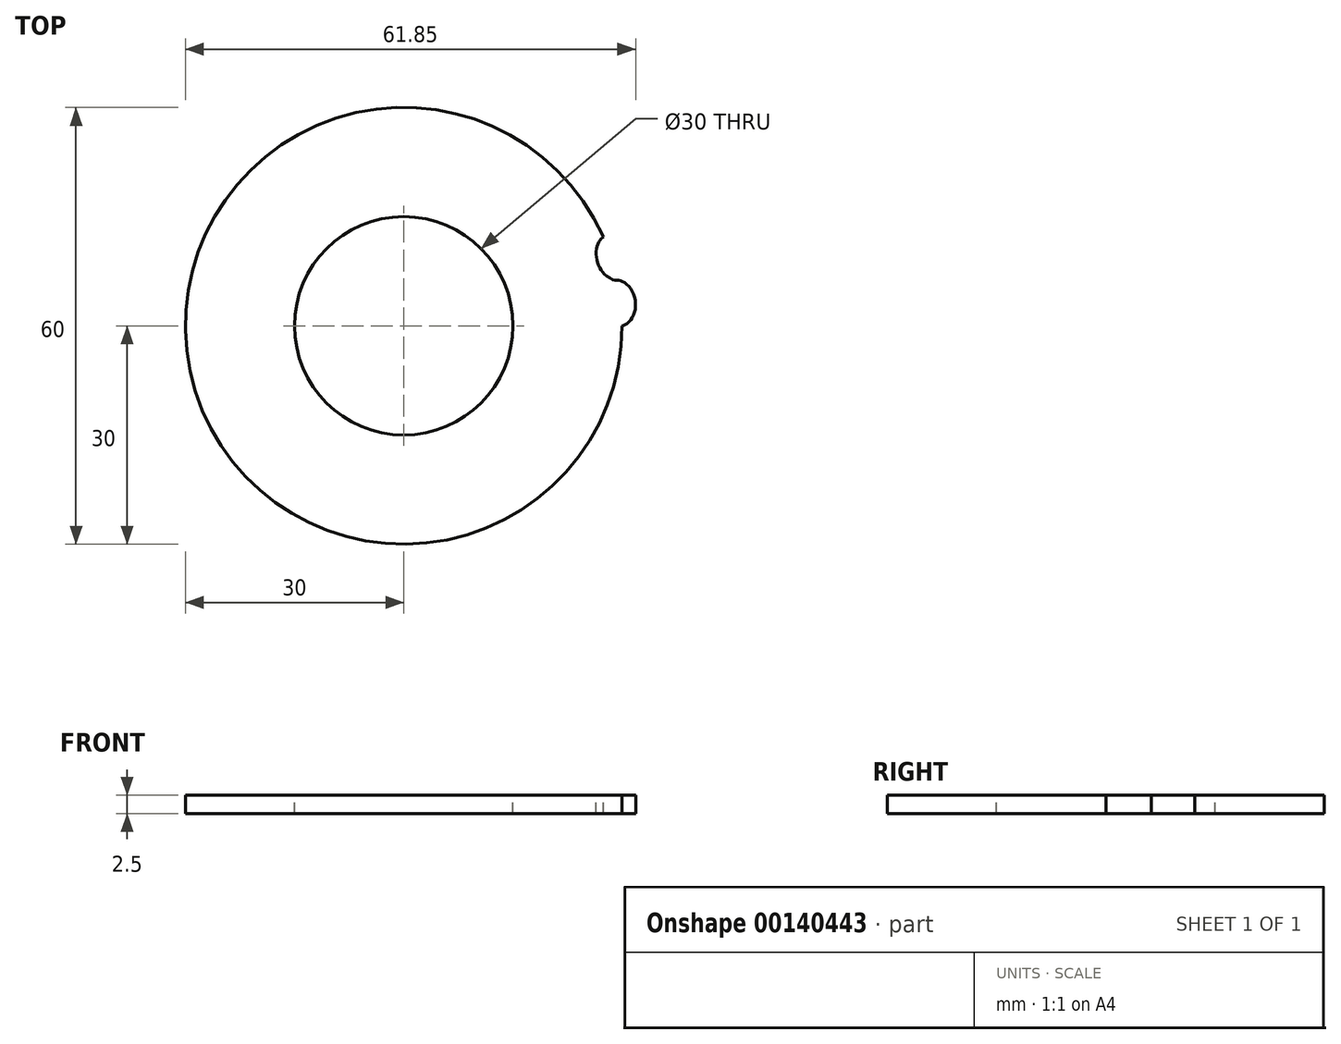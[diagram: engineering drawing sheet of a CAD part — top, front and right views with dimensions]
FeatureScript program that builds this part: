
annotation { "Feature Type Name" : "Feature", "Feature Type Description" : "" }
export const myFeature = defineFeature(function(context is Context, id is Id, definition is map)
    precondition{}
    {
        {
            assignVariable(context, id + "F0", {"name" : "t", "anyValue" : 2.5});
        }
        {
            var Q0;
            Q0=qCreatedBy(makeId("Top.planeOp"),FACE);
            var sketch = newSketch(context, id + "F1", { "sketchPlane" : qUnion([Q0])});
            skCircle(sketch, "E0", {"center": v(0, 0) * mm, "radius": 30 * mm});
            skSolve(sketch);
        }
        {
            var Q0;
            Q0 = qSketchRegion(id + "F1", true);
            extrude(context, id + "F2", {"entities" : qUnion([Q0]), "depth" : (getVariable(context, 't')) * mm});
        }
        {
            var Q0;
            Q0=makeQuery(id+"F2.opExtrude","CAP_FACE",FACE,{"disambiguationData":[OSD([sQuery(id+"F1.wireOp",EDGE,"E0")])],"isStart":false});
            var sketch = newSketch(context, id + "F3", { "sketchPlane" : qUnion([Q0])});
            skLineSegment(sketch, "E1", {"start": v(0, 0) * mm, "end": v(29.34, 6.24) * mm, "construction": true});
            skLineSegment(sketch, "E2", {"start": v(29.34, 6.24) * mm, "end": v(31.3, 6.65) * mm, "construction": true});
            skPoint(sketch, "E3", {"position": v(30.32, 6.45) * mm});
            skCircle(sketch, "E4", {"center": v(30.32, 6.45) * mm, "radius": 1 * mm, "construction": true});
            skLineSegment(sketch, "E5", {"start": v(30, 0) * mm, "end": v(31, 0) * mm, "construction": true});
            skLineSegment(sketch, "E6", {"start": v(30.32, 6.45) * mm, "end": v(29.58, 5.78) * mm, "construction": true});
            skLineSegment(sketch, "E7", {"start": v(30.32, 6.45) * mm, "end": v(31.07, 7.11) * mm, "construction": true});
            skLineSegment(sketch, "E8", {"start": v(30.32, 6.45) * mm, "end": v(29.37, 6.75) * mm, "construction": true});
            skLineSegment(sketch, "E9", {"start": v(30.32, 6.45) * mm, "end": v(31.27, 6.14) * mm, "construction": true});
            skLineSegment(sketch, "E10", {"start": v(30.32, 6.45) * mm, "end": v(30.01, 5.5) * mm, "construction": true});
            skLineSegment(sketch, "E11", {"start": v(30.32, 6.45) * mm, "end": v(30.53, 5.47) * mm, "construction": true});
            skLineSegment(sketch, "E12", {"start": v(30.32, 6.45) * mm, "end": v(31, 5.7) * mm, "construction": true});
            skLineSegment(sketch, "E13", {"start": v(30.32, 6.45) * mm, "end": v(30.63, 7.4) * mm, "construction": true});
            skLineSegment(sketch, "E14", {"start": v(30.32, 6.45) * mm, "end": v(30.11, 7.42) * mm, "construction": true});
            skLineSegment(sketch, "E15", {"start": v(30.32, 6.45) * mm, "end": v(29.65, 7.19) * mm, "construction": true});
            skArc(sketch, "E16", {"start": v(31, 0) * mm, "mid": v(30.83, 3.24) * mm, "end": v(30.32, 6.45) * mm, "construction": true});
            skLineSegment(sketch, "E17", {"start": v(30.43, 5.92) * mm, "end": v(0, 0) * mm, "construction": true});
            skLineSegment(sketch, "E18", {"start": v(0, 0) * mm, "end": v(30.53, 5.38) * mm, "construction": true});
            skLineSegment(sketch, "E19", {"start": v(0, 0) * mm, "end": v(30.62, 4.85) * mm, "construction": true});
            skLineSegment(sketch, "E20", {"start": v(0, 0) * mm, "end": v(30.7, 4.31) * mm, "construction": true});
            skLineSegment(sketch, "E21", {"start": v(0, 0) * mm, "end": v(30.77, 3.78) * mm, "construction": true});
            skLineSegment(sketch, "E22", {"start": v(0, 0) * mm, "end": v(30.83, 3.24) * mm, "construction": true});
            skLineSegment(sketch, "E23", {"start": v(0, 0) * mm, "end": v(30.88, 2.7) * mm, "construction": true});
            skLineSegment(sketch, "E24", {"start": v(0, 0) * mm, "end": v(30.92, 2.16) * mm, "construction": true});
            skLineSegment(sketch, "E25", {"start": v(0, 0) * mm, "end": v(30.96, 1.62) * mm, "construction": true});
            skLineSegment(sketch, "E26", {"start": v(0, 0) * mm, "end": v(30.98, 1.08) * mm, "construction": true});
            skLineSegment(sketch, "E27", {"start": v(0, 0) * mm, "end": v(31, 0.54) * mm, "construction": true});
            skLineSegment(sketch, "E28", {"start": v(0, 0) * mm, "end": v(31, 0) * mm, "construction": true});
            skLineSegment(sketch, "E29", {"start": v(31, 0) * mm, "end": v(31.87, 0) * mm, "construction": true});
            skArc(sketch, "E30", {"start": v(29.37, 6.75) * mm, "mid": v(29.95, 3.4) * mm, "end": v(30.14, 0) * mm, "construction": true});
            skArc(sketch, "E31", {"start": v(29.65, 7.19) * mm, "mid": v(30.3, 3.62) * mm, "end": v(30.51, 0) * mm, "construction": true});
            skArc(sketch, "E32", {"start": v(30.11, 7.42) * mm, "mid": v(30.79, 3.74) * mm, "end": v(31.02, 0) * mm, "construction": true});
            skArc(sketch, "E33", {"start": v(30.63, 7.4) * mm, "mid": v(31.3, 3.72) * mm, "end": v(31.51, 0) * mm, "construction": true});
            skArc(sketch, "E34", {"start": v(31.07, 7.11) * mm, "mid": v(31.67, 3.58) * mm, "end": v(31.87, 0) * mm, "construction": true});
            skPoint(sketch, "E35", {"position": v(29.95, 5.82) * mm});
            skPoint(sketch, "E36", {"position": v(30.43, 5.92) * mm});
            skLineSegment(sketch, "E37", {"start": v(30.43, 5.92) * mm, "end": v(29.48, 6.24) * mm, "construction": true});
            skLineSegment(sketch, "E38", {"start": v(30.53, 5.38) * mm, "end": v(29.89, 6.15) * mm, "construction": true});
            skLineSegment(sketch, "E39", {"start": v(30.62, 4.85) * mm, "end": v(30.46, 5.84) * mm, "construction": true});
            skLineSegment(sketch, "E40", {"start": v(30.7, 4.31) * mm, "end": v(31.07, 5.24) * mm, "construction": true});
            skArc(sketch, "E41", {"start": v(31.3, 6.65) * mm, "mid": v(31.82, 3.34) * mm, "end": v(32, 0) * mm, "construction": true});
            skLineSegment(sketch, "E42", {"start": v(30.77, 3.78) * mm, "end": v(31.57, 4.38) * mm, "construction": true});
            skLineSegment(sketch, "E43", {"start": v(30.83, 3.24) * mm, "end": v(31.82, 3.34) * mm, "construction": true});
            skLineSegment(sketch, "E44", {"start": v(30.88, 2.7) * mm, "end": v(31.79, 2.28) * mm, "construction": true});
            skLineSegment(sketch, "E45", {"start": v(30.92, 2.16) * mm, "end": v(31.48, 1.33) * mm, "construction": true});
            skLineSegment(sketch, "E46", {"start": v(30.96, 1.62) * mm, "end": v(31, 0.62) * mm, "construction": true});
            skLineSegment(sketch, "E47", {"start": v(30.98, 1.08) * mm, "end": v(30.51, 0.2) * mm, "construction": true});
            skLineSegment(sketch, "E48", {"start": v(31, 0.54) * mm, "end": v(30.14, 0.03) * mm, "construction": true});
            skFitSpline(sketch, "E49", {"points": [v(29.34, 6.24) * mm, v(29.48, 6.24) * mm, v(29.89, 6.15) * mm, v(30.46, 5.84) * mm, v(31.07, 5.24) * mm, v(31.57, 4.38) * mm, v(31.82, 3.34) * mm, v(31.79, 2.28) * mm, v(31.48, 1.33) * mm, v(31, 0.62) * mm, v(30.51, 0.2) * mm, v(30.14, 0.03) * mm, v(30, 0) * mm], "startDerivative": vector(3.74, 0.8) * mm, "endDerivative": vector(-3.82, 0) * mm});
            skArc(sketch, "E50.0", {"start": v(30, 0) * mm, "mid": v(29.84, 3.14) * mm, "end": v(29.34, 6.24) * mm});
            skArc(sketch, "E51", {"start": v(29.34, 6.24) * mm, "mid": v(29.4, 5.98) * mm, "end": v(29.45, 5.72) * mm});
            skArc(sketch, "E52", {"start": v(29.45, 5.72) * mm, "mid": v(29.5, 5.47) * mm, "end": v(29.54, 5.2) * mm});
            skLineSegment(sketch, "E53", {"start": v(-26.75, -3.74) * mm, "end": v(2.6, 2.5) * mm, "construction": true});
            skLineSegment(sketch, "E54", {"start": v(2.6, 2.5) * mm, "end": v(4.55, 2.91) * mm, "construction": true});
            skPoint(sketch, "E55", {"position": v(3.58, 2.7) * mm});
            skCircle(sketch, "E56", {"center": v(3.58, 2.7) * mm, "radius": 1 * mm, "construction": true});
            skLineSegment(sketch, "E57", {"start": v(3.25, -3.74) * mm, "end": v(4.25, -3.74) * mm, "construction": true});
            skLineSegment(sketch, "E58", {"start": v(3.58, 2.7) * mm, "end": v(2.83, 2.04) * mm, "construction": true});
            skLineSegment(sketch, "E59", {"start": v(3.58, 2.7) * mm, "end": v(4.32, 3.37) * mm, "construction": true});
            skLineSegment(sketch, "E60", {"start": v(3.58, 2.7) * mm, "end": v(2.62, 3.01) * mm, "construction": true});
            skLineSegment(sketch, "E61", {"start": v(3.58, 2.7) * mm, "end": v(4.53, 2.4) * mm, "construction": true});
            skLineSegment(sketch, "E62", {"start": v(3.58, 2.7) * mm, "end": v(3.27, 1.75) * mm, "construction": true});
            skLineSegment(sketch, "E63", {"start": v(3.58, 2.7) * mm, "end": v(3.78, 1.73) * mm, "construction": true});
            skLineSegment(sketch, "E64", {"start": v(3.58, 2.7) * mm, "end": v(4.24, 1.96) * mm, "construction": true});
            skLineSegment(sketch, "E65", {"start": v(3.58, 2.7) * mm, "end": v(3.88, 3.66) * mm, "construction": true});
            skLineSegment(sketch, "E66", {"start": v(3.58, 2.7) * mm, "end": v(3.37, 3.68) * mm, "construction": true});
            skLineSegment(sketch, "E67", {"start": v(3.58, 2.7) * mm, "end": v(2.9, 3.45) * mm, "construction": true});
            skArc(sketch, "E68", {"start": v(4.25, -3.74) * mm, "mid": v(4.08, -0.5) * mm, "end": v(3.58, 2.7) * mm, "construction": true});
            skLineSegment(sketch, "E69", {"start": v(3.68, 2.17) * mm, "end": v(-26.75, -3.74) * mm, "construction": true});
            skLineSegment(sketch, "E70", {"start": v(-26.75, -3.74) * mm, "end": v(3.78, 1.64) * mm, "construction": true});
            skLineSegment(sketch, "E71", {"start": v(-26.75, -3.74) * mm, "end": v(3.87, 1.1) * mm, "construction": true});
            skLineSegment(sketch, "E72", {"start": v(-26.75, -3.74) * mm, "end": v(3.95, 0.57) * mm, "construction": true});
            skLineSegment(sketch, "E73", {"start": v(-26.75, -3.74) * mm, "end": v(4.02, 0.04) * mm, "construction": true});
            skLineSegment(sketch, "E74", {"start": v(-26.75, -3.74) * mm, "end": v(4.08, -0.5) * mm, "construction": true});
            skLineSegment(sketch, "E75", {"start": v(-26.75, -3.74) * mm, "end": v(4.13, -1.04) * mm, "construction": true});
            skLineSegment(sketch, "E76", {"start": v(-26.75, -3.74) * mm, "end": v(4.18, -1.58) * mm, "construction": true});
            skLineSegment(sketch, "E77", {"start": v(-26.75, -3.74) * mm, "end": v(4.2, -2.12) * mm, "construction": true});
            skLineSegment(sketch, "E78", {"start": v(-26.75, -3.74) * mm, "end": v(4.23, -2.66) * mm, "construction": true});
            skLineSegment(sketch, "E79", {"start": v(-26.75, -3.74) * mm, "end": v(4.25, -3.2) * mm, "construction": true});
            skLineSegment(sketch, "E80", {"start": v(-26.75, -3.74) * mm, "end": v(4.25, -3.74) * mm, "construction": true});
            skLineSegment(sketch, "E81", {"start": v(4.25, -3.74) * mm, "end": v(5.12, -3.74) * mm, "construction": true});
            skArc(sketch, "E82", {"start": v(2.62, 3.01) * mm, "mid": v(3.2, -0.34) * mm, "end": v(3.4, -3.74) * mm, "construction": true});
            skArc(sketch, "E83", {"start": v(2.9, 3.45) * mm, "mid": v(3.55, -0.12) * mm, "end": v(3.76, -3.74) * mm, "construction": true});
            skArc(sketch, "E84", {"start": v(3.37, 3.68) * mm, "mid": v(4.04, 0) * mm, "end": v(4.27, -3.74) * mm, "construction": true});
            skArc(sketch, "E85", {"start": v(3.88, 3.66) * mm, "mid": v(4.54, -0.02) * mm, "end": v(4.76, -3.74) * mm, "construction": true});
            skArc(sketch, "E86", {"start": v(4.32, 3.37) * mm, "mid": v(4.92, -0.16) * mm, "end": v(5.12, -3.74) * mm, "construction": true});
            skPoint(sketch, "E87", {"position": v(3.2, 2.08) * mm});
            skPoint(sketch, "E88", {"position": v(3.68, 2.17) * mm});
            skLineSegment(sketch, "E89", {"start": v(3.68, 2.17) * mm, "end": v(2.74, 2.5) * mm, "construction": true});
            skLineSegment(sketch, "E90", {"start": v(3.78, 1.64) * mm, "end": v(3.14, 2.4) * mm, "construction": true});
            skLineSegment(sketch, "E91", {"start": v(3.87, 1.1) * mm, "end": v(3.71, 2.1) * mm, "construction": true});
            skLineSegment(sketch, "E92", {"start": v(3.95, 0.57) * mm, "end": v(4.33, 1.5) * mm, "construction": true});
            skArc(sketch, "E93", {"start": v(4.55, 2.91) * mm, "mid": v(5.08, -0.4) * mm, "end": v(5.25, -3.74) * mm, "construction": true});
            skLineSegment(sketch, "E94", {"start": v(4.02, 0.04) * mm, "end": v(4.82, 0.64) * mm, "construction": true});
            skLineSegment(sketch, "E95", {"start": v(4.08, -0.5) * mm, "end": v(5.08, -0.4) * mm, "construction": true});
            skLineSegment(sketch, "E96", {"start": v(4.13, -1.04) * mm, "end": v(5.04, -1.46) * mm, "construction": true});
            skLineSegment(sketch, "E97", {"start": v(4.18, -1.58) * mm, "end": v(4.74, -2.4) * mm, "construction": true});
            skLineSegment(sketch, "E98", {"start": v(4.2, -2.12) * mm, "end": v(4.26, -3.12) * mm, "construction": true});
            skLineSegment(sketch, "E99", {"start": v(4.23, -2.66) * mm, "end": v(3.76, -3.54) * mm, "construction": true});
            skLineSegment(sketch, "E100", {"start": v(4.25, -3.2) * mm, "end": v(3.4, -3.71) * mm, "construction": true});
            skFitSpline(sketch, "E101", {"points": [v(2.6, 2.5) * mm, v(2.74, 2.5) * mm, v(3.14, 2.4) * mm, v(3.71, 2.1) * mm, v(4.33, 1.5) * mm, v(4.82, 0.64) * mm, v(5.08, -0.4) * mm, v(5.04, -1.46) * mm, v(4.74, -2.4) * mm, v(4.26, -3.12) * mm, v(3.76, -3.54) * mm, v(3.4, -3.71) * mm, v(3.25, -3.74) * mm], "startDerivative": vector(3.74, 0.8) * mm, "endDerivative": vector(-3.82, 0) * mm});
            skArc(sketch, "E102.0", {"start": v(3.25, -3.74) * mm, "mid": v(3.09, -0.6) * mm, "end": v(2.6, 2.5) * mm});
            skArc(sketch, "E103", {"start": v(2.6, 2.5) * mm, "mid": v(2.65, 2.24) * mm, "end": v(2.7, 1.98) * mm});
            skArc(sketch, "E104", {"start": v(2.7, 1.98) * mm, "mid": v(2.75, 1.73) * mm, "end": v(2.8, 1.47) * mm});
            skSolve(sketch);
        }
        {
            var Q0;
            Q0 = qSketchRegion(id + "F3", true);
            var Q1;
            Q1=makeQuery(id+"F2.opExtrude","CAP_FACE",FACE,{"disambiguationData":[OSD([sQuery(id+"F1.wireOp",EDGE,"E0")])],"isStart":true});
            extrude(context, id + "F4", {"entities" : qUnion([Q0]), "operationType" : NewBodyOperationType.ADD, "endBound" : BoundingType.UP_TO_SURFACE, "oppositeDirection" : true, "endBoundEntityFace" : qUnion([Q1]), "depth" : 2.5 * mm});
        }
        {
            var Q0;
            {var subQ0=sQuery(id+"F3.wireOp",EDGE,"E50.0");Q0=makeQuery(id+"F3.imprint","IMPRINT",FACE,{"disambiguationData":[TD([[makeQuery(id+"F3.imprint","IMPRINT",EDGE,{"derivedFrom":subQ0}),1.0]])]});}
            var sketch = newSketch(context, id + "F5", { "sketchPlane" : qUnion([Q0])});
            skLineSegment(sketch, "E105.0", {"start": v(0, 0) * mm, "end": v(29.34, 6.24) * mm, "construction": true});
            skLineSegment(sketch, "E106.0.0", {"start": v(30, 0) * mm, "end": v(30, 0) * mm});
            skLineSegment(sketch, "E107", {"start": v(0, 0) * mm, "end": v(27.4, 12.2) * mm, "construction": true});
            skCircle(sketch, "E108", {"center": v(26.5, 11.8) * mm, "radius": 1 * mm, "construction": true});
            skArc(sketch, "E109", {"start": v(26.5, 11.8) * mm, "mid": v(27.58, 8.96) * mm, "end": v(28.37, 6.03) * mm, "construction": true});
            skLineSegment(sketch, "E110", {"start": v(26.5, 11.8) * mm, "end": v(26.9, 10.88) * mm, "construction": true});
            skArc(sketch, "E111", {"start": v(27.08, 12.6) * mm, "mid": v(28.33, 9.47) * mm, "end": v(29.22, 6.21) * mm, "construction": true});
            skArc(sketch, "E112", {"start": v(26.6, 12.79) * mm, "mid": v(27.93, 9.53) * mm, "end": v(28.87, 6.14) * mm, "construction": true});
            skArc(sketch, "E113", {"start": v(25.68, 12.38) * mm, "mid": v(26.98, 9.22) * mm, "end": v(27.9, 5.93) * mm, "construction": true});
            skArc(sketch, "E114", {"start": v(25.5, 11.9) * mm, "mid": v(26.68, 8.93) * mm, "end": v(27.52, 5.85) * mm, "construction": true});
            skArc(sketch, "E115", {"start": v(27.4, 12.2) * mm, "mid": v(27.51, 11.96) * mm, "end": v(27.62, 11.72) * mm});
            skLineSegment(sketch, "E116", {"start": v(27.62, 11.72) * mm, "end": v(0, 0) * mm, "construction": true});
            skArc(sketch, "E117", {"start": v(27.4, 12.2) * mm, "mid": v(28.53, 9.27) * mm, "end": v(29.34, 6.24) * mm});
            skLineSegment(sketch, "E118", {"start": v(0, 0) * mm, "end": v(27.82, 11.24) * mm, "construction": true});
            skLineSegment(sketch, "E119", {"start": v(0, 0) * mm, "end": v(28, 10.75) * mm, "construction": true});
            skLineSegment(sketch, "E120", {"start": v(0, 0) * mm, "end": v(28.2, 10.26) * mm, "construction": true});
            skLineSegment(sketch, "E121", {"start": v(0, 0) * mm, "end": v(28.37, 9.77) * mm, "construction": true});
            skLineSegment(sketch, "E122", {"start": v(0, 0) * mm, "end": v(28.53, 9.27) * mm, "construction": true});
            skLineSegment(sketch, "E123", {"start": v(0, 0) * mm, "end": v(28.69, 8.77) * mm, "construction": true});
            skLineSegment(sketch, "E124", {"start": v(0, 0) * mm, "end": v(28.84, 8.27) * mm, "construction": true});
            skLineSegment(sketch, "E125", {"start": v(28.98, 7.76) * mm, "end": v(0, 0) * mm, "construction": true});
            skLineSegment(sketch, "E126", {"start": v(0, 0) * mm, "end": v(29.1, 7.26) * mm, "construction": true});
            skLineSegment(sketch, "E127", {"start": v(0, 0) * mm, "end": v(29.23, 6.75) * mm, "construction": true});
            skLineSegment(sketch, "E128", {"start": v(26.7, 11.33) * mm, "end": v(27.3, 12.13) * mm, "construction": true});
            skLineSegment(sketch, "E129", {"start": v(26.89, 10.86) * mm, "end": v(27.03, 11.85) * mm, "construction": true});
            skArc(sketch, "E130", {"start": v(26.09, 12.7) * mm, "mid": v(27.44, 9.44) * mm, "end": v(28.38, 6.03) * mm, "construction": true});
            skLineSegment(sketch, "E131", {"start": v(27.07, 10.4) * mm, "end": v(26.72, 11.33) * mm, "construction": true});
            skLineSegment(sketch, "E132", {"start": v(27.25, 9.92) * mm, "end": v(26.49, 10.56) * mm, "construction": true});
            skLineSegment(sketch, "E133", {"start": v(27.42, 9.44) * mm, "end": v(26.44, 9.63) * mm, "construction": true});
            skLineSegment(sketch, "E134", {"start": v(27.58, 8.96) * mm, "end": v(26.63, 8.65) * mm, "construction": true});
            skArc(sketch, "E135", {"start": v(25.58, 11.39) * mm, "mid": v(26.63, 8.65) * mm, "end": v(27.39, 5.82) * mm, "construction": true});
            skLineSegment(sketch, "E136", {"start": v(27.73, 8.48) * mm, "end": v(27.05, 7.75) * mm, "construction": true});
            skLineSegment(sketch, "E137", {"start": v(27.88, 8) * mm, "end": v(27.63, 7.02) * mm, "construction": true});
            skLineSegment(sketch, "E138", {"start": v(28.14, 7.02) * mm, "end": v(28.83, 6.3) * mm, "construction": true});
            skLineSegment(sketch, "E139", {"start": v(28.26, 6.52) * mm, "end": v(29.21, 6.23) * mm, "construction": true});
            skFitSpline(sketch, "E140", {"points": [v(29.34, 6.24) * mm, v(29.21, 6.23) * mm, v(28.83, 6.3) * mm, v(27.63, 7.02) * mm, v(27.05, 7.75) * mm, v(26.63, 8.65) * mm, v(26.44, 9.63) * mm, v(26.49, 10.56) * mm, v(26.72, 11.33) * mm, v(27.03, 11.85) * mm, v(27.3, 12.13) * mm, v(27.4, 12.2) * mm], "startDerivative": vector(-3.54, -0.75) * mm, "endDerivative": vector(3.3, 1.47) * mm});
            skLineSegment(sketch, "E141", {"start": v(26.5, 11.8) * mm, "end": v(27.08, 12.6) * mm, "construction": true});
            skLineSegment(sketch, "E142", {"start": v(26.5, 11.8) * mm, "end": v(26.6, 12.79) * mm, "construction": true});
            skLineSegment(sketch, "E143", {"start": v(26.5, 11.8) * mm, "end": v(26.09, 12.7) * mm, "construction": true});
            skLineSegment(sketch, "E144", {"start": v(26.5, 11.8) * mm, "end": v(25.68, 12.38) * mm, "construction": true});
            skLineSegment(sketch, "E145", {"start": v(26.5, 11.8) * mm, "end": v(25.5, 11.9) * mm, "construction": true});
            skSolve(sketch);
        }
        {
            var Q0;
            Q0 = qSketchRegion(id + "F5", true);
            extrude(context, id + "F6", {"entities" : qUnion([Q0]), "operationType" : NewBodyOperationType.REMOVE, "endBound" : BoundingType.THROUGH_ALL, "oppositeDirection" : true, "depth" : 25 * mm});
        }
        {
            var Q0;
            {var subQ0=sQuery(id+"F3.wireOp",EDGE,"E52");var subQ1=sQuery(id+"F3.wireOp",EDGE,"E51");var subQ2=sQuery(id+"F3.wireOp",EDGE,"E50.0");var subQ3=sQuery(id+"F3.wireOp",EDGE,"E49");Q0=makeQuery(id+"FYuu5osC36glpG0_1.29.F4.boolean.opBoolean","MERGE",FACE,{"derivedFrom":[makeQuery(id+"FYuu5osC36glpG0_1.28.F4.boolean.opBoolean","MERGE",FACE,{"derivedFrom":[makeQuery(id+"FYuu5osC36glpG0_1.27.F4.boolean.opBoolean","MERGE",FACE,{"derivedFrom":[makeQuery(id+"FYuu5osC36glpG0_1.26.F4.boolean.opBoolean","MERGE",FACE,{"derivedFrom":[makeQuery(id+"FYuu5osC36glpG0_1.25.F4.boolean.opBoolean","MERGE",FACE,{"derivedFrom":[makeQuery(id+"FYuu5osC36glpG0_1.24.F4.boolean.opBoolean","MERGE",FACE,{"derivedFrom":[makeQuery(id+"FYuu5osC36glpG0_1.23.F4.boolean.opBoolean","MERGE",FACE,{"derivedFrom":[makeQuery(id+"FYuu5osC36glpG0_1.22.F4.boolean.opBoolean","MERGE",FACE,{"derivedFrom":[makeQuery(id+"FYuu5osC36glpG0_1.21.F4.boolean.opBoolean","MERGE",FACE,{"derivedFrom":[makeQuery(id+"FYuu5osC36glpG0_1.20.F4.boolean.opBoolean","MERGE",FACE,{"derivedFrom":[makeQuery(id+"FYuu5osC36glpG0_1.19.F4.boolean.opBoolean","MERGE",FACE,{"derivedFrom":[makeQuery(id+"FYuu5osC36glpG0_1.18.F4.boolean.opBoolean","MERGE",FACE,{"derivedFrom":[makeQuery(id+"FYuu5osC36glpG0_1.17.F4.boolean.opBoolean","MERGE",FACE,{"derivedFrom":[makeQuery(id+"FYuu5osC36glpG0_1.16.F4.boolean.opBoolean","MERGE",FACE,{"derivedFrom":[makeQuery(id+"FYuu5osC36glpG0_1.15.F4.boolean.opBoolean","MERGE",FACE,{"derivedFrom":[makeQuery(id+"FYuu5osC36glpG0_1.14.F4.boolean.opBoolean","MERGE",FACE,{"derivedFrom":[makeQuery(id+"FYuu5osC36glpG0_1.13.F4.boolean.opBoolean","MERGE",FACE,{"derivedFrom":[makeQuery(id+"FYuu5osC36glpG0_1.12.F4.boolean.opBoolean","MERGE",FACE,{"derivedFrom":[makeQuery(id+"FYuu5osC36glpG0_1.11.F4.boolean.opBoolean","MERGE",FACE,{"derivedFrom":[makeQuery(id+"FYuu5osC36glpG0_1.10.F4.boolean.opBoolean","MERGE",FACE,{"derivedFrom":[makeQuery(id+"FYuu5osC36glpG0_1.9.F4.boolean.opBoolean","MERGE",FACE,{"derivedFrom":[makeQuery(id+"FYuu5osC36glpG0_1.8.F4.boolean.opBoolean","MERGE",FACE,{"derivedFrom":[makeQuery(id+"FYuu5osC36glpG0_1.7.F4.boolean.opBoolean","MERGE",FACE,{"derivedFrom":[makeQuery(id+"FYuu5osC36glpG0_1.6.F4.boolean.opBoolean","MERGE",FACE,{"derivedFrom":[makeQuery(id+"FYuu5osC36glpG0_1.5.F4.boolean.opBoolean","MERGE",FACE,{"derivedFrom":[makeQuery(id+"FYuu5osC36glpG0_1.4.F4.boolean.opBoolean","MERGE",FACE,{"derivedFrom":[makeQuery(id+"FYuu5osC36glpG0_1.3.F4.boolean.opBoolean","MERGE",FACE,{"derivedFrom":[makeQuery(id+"FYuu5osC36glpG0_1.2.F4.boolean.opBoolean","MERGE",FACE,{"derivedFrom":[makeQuery(id+"FYuu5osC36glpG0_1.1.F4.boolean.opBoolean","MERGE",FACE,{"derivedFrom":[makeQuery(id+"F4.boolean.opBoolean","MERGE",FACE,{"derivedFrom":[makeQuery(id+"F2.opExtrude","CAP_FACE",FACE,{"disambiguationData":[OSD([sQuery(id+"F1.wireOp",EDGE,"E0")])],"isStart":false}),makeQuery(id+"F4.opExtrude","CAP_FACE",FACE,{"disambiguationData":[OSD([subQ3,subQ2,subQ1,subQ0])],"isStart":true})]}),makeQuery(id+"FYuu5osC36glpG0_1.1.F4.opExtrude","CAP_FACE",FACE,{"disambiguationData":[OSD([subQ3,subQ2,subQ1,subQ0])],"isStart":true})]}),makeQuery(id+"FYuu5osC36glpG0_1.2.F4.opExtrude","CAP_FACE",FACE,{"disambiguationData":[OSD([subQ3,subQ2,subQ1,subQ0])],"isStart":true})]}),makeQuery(id+"FYuu5osC36glpG0_1.3.F4.opExtrude","CAP_FACE",FACE,{"disambiguationData":[OSD([subQ3,subQ2,subQ1,subQ0])],"isStart":true})]}),makeQuery(id+"FYuu5osC36glpG0_1.4.F4.opExtrude","CAP_FACE",FACE,{"disambiguationData":[OSD([subQ3,subQ2,subQ1,subQ0])],"isStart":true})]}),makeQuery(id+"FYuu5osC36glpG0_1.5.F4.opExtrude","CAP_FACE",FACE,{"disambiguationData":[OSD([subQ3,subQ2,subQ1,subQ0])],"isStart":true})]}),makeQuery(id+"FYuu5osC36glpG0_1.6.F4.opExtrude","CAP_FACE",FACE,{"disambiguationData":[OSD([subQ3,subQ2,subQ1,subQ0])],"isStart":true})]}),makeQuery(id+"FYuu5osC36glpG0_1.7.F4.opExtrude","CAP_FACE",FACE,{"disambiguationData":[OSD([subQ3,subQ2,subQ1,subQ0])],"isStart":true})]}),makeQuery(id+"FYuu5osC36glpG0_1.8.F4.opExtrude","CAP_FACE",FACE,{"disambiguationData":[OSD([subQ3,subQ2,subQ1,subQ0])],"isStart":true})]}),makeQuery(id+"FYuu5osC36glpG0_1.9.F4.opExtrude","CAP_FACE",FACE,{"disambiguationData":[OSD([subQ3,subQ2,subQ1,subQ0])],"isStart":true})]}),makeQuery(id+"FYuu5osC36glpG0_1.10.F4.opExtrude","CAP_FACE",FACE,{"disambiguationData":[OSD([subQ3,subQ2,subQ1,subQ0])],"isStart":true})]}),makeQuery(id+"FYuu5osC36glpG0_1.11.F4.opExtrude","CAP_FACE",FACE,{"disambiguationData":[OSD([subQ3,subQ2,subQ1,subQ0])],"isStart":true})]}),makeQuery(id+"FYuu5osC36glpG0_1.12.F4.opExtrude","CAP_FACE",FACE,{"disambiguationData":[OSD([subQ3,subQ2,subQ1,subQ0])],"isStart":true})]}),makeQuery(id+"FYuu5osC36glpG0_1.13.F4.opExtrude","CAP_FACE",FACE,{"disambiguationData":[OSD([subQ3,subQ2,subQ1,subQ0])],"isStart":true})]}),makeQuery(id+"FYuu5osC36glpG0_1.14.F4.opExtrude","CAP_FACE",FACE,{"disambiguationData":[OSD([subQ3,subQ2,subQ1,subQ0])],"isStart":true})]}),makeQuery(id+"FYuu5osC36glpG0_1.15.F4.opExtrude","CAP_FACE",FACE,{"disambiguationData":[OSD([subQ3,subQ2,subQ1,subQ0])],"isStart":true})]}),makeQuery(id+"FYuu5osC36glpG0_1.16.F4.opExtrude","CAP_FACE",FACE,{"disambiguationData":[OSD([subQ3,subQ2,subQ1,subQ0])],"isStart":true})]}),makeQuery(id+"FYuu5osC36glpG0_1.17.F4.opExtrude","CAP_FACE",FACE,{"disambiguationData":[OSD([subQ3,subQ2,subQ1,subQ0])],"isStart":true})]}),makeQuery(id+"FYuu5osC36glpG0_1.18.F4.opExtrude","CAP_FACE",FACE,{"disambiguationData":[OSD([subQ3,subQ2,subQ1,subQ0])],"isStart":true})]}),makeQuery(id+"FYuu5osC36glpG0_1.19.F4.opExtrude","CAP_FACE",FACE,{"disambiguationData":[OSD([subQ3,subQ2,subQ1,subQ0])],"isStart":true})]}),makeQuery(id+"FYuu5osC36glpG0_1.20.F4.opExtrude","CAP_FACE",FACE,{"disambiguationData":[OSD([subQ3,subQ2,subQ1,subQ0])],"isStart":true})]}),makeQuery(id+"FYuu5osC36glpG0_1.21.F4.opExtrude","CAP_FACE",FACE,{"disambiguationData":[OSD([subQ3,subQ2,subQ1,subQ0])],"isStart":true})]}),makeQuery(id+"FYuu5osC36glpG0_1.22.F4.opExtrude","CAP_FACE",FACE,{"disambiguationData":[OSD([subQ3,subQ2,subQ1,subQ0])],"isStart":true})]}),makeQuery(id+"FYuu5osC36glpG0_1.23.F4.opExtrude","CAP_FACE",FACE,{"disambiguationData":[OSD([subQ3,subQ2,subQ1,subQ0])],"isStart":true})]}),makeQuery(id+"FYuu5osC36glpG0_1.24.F4.opExtrude","CAP_FACE",FACE,{"disambiguationData":[OSD([subQ3,subQ2,subQ1,subQ0])],"isStart":true})]}),makeQuery(id+"FYuu5osC36glpG0_1.25.F4.opExtrude","CAP_FACE",FACE,{"disambiguationData":[OSD([subQ3,subQ2,subQ1,subQ0])],"isStart":true})]}),makeQuery(id+"FYuu5osC36glpG0_1.26.F4.opExtrude","CAP_FACE",FACE,{"disambiguationData":[OSD([subQ3,subQ2,subQ1,subQ0])],"isStart":true})]}),makeQuery(id+"FYuu5osC36glpG0_1.27.F4.opExtrude","CAP_FACE",FACE,{"disambiguationData":[OSD([subQ3,subQ2,subQ1,subQ0])],"isStart":true})]}),makeQuery(id+"FYuu5osC36glpG0_1.28.F4.opExtrude","CAP_FACE",FACE,{"disambiguationData":[OSD([subQ3,subQ2,subQ1,subQ0])],"isStart":true})]}),makeQuery(id+"FYuu5osC36glpG0_1.29.F4.opExtrude","CAP_FACE",FACE,{"disambiguationData":[OSD([subQ3,subQ2,subQ1,subQ0])],"isStart":true})]});}
            var sketch = newSketch(context, id + "F7", { "sketchPlane" : qUnion([Q0])});
            skCircle(sketch, "E146", {"center": v(0, 0) * mm, "radius": 15 * mm});
            skSolve(sketch);
        }
        {
            var Q0;
            Q0 = qSketchRegion(id + "F7", true);
            extrude(context, id + "F8", {"entities" : qUnion([Q0]), "operationType" : NewBodyOperationType.REMOVE, "endBound" : BoundingType.THROUGH_ALL, "oppositeDirection" : true, "depth" : 25 * mm});
        }
    });
